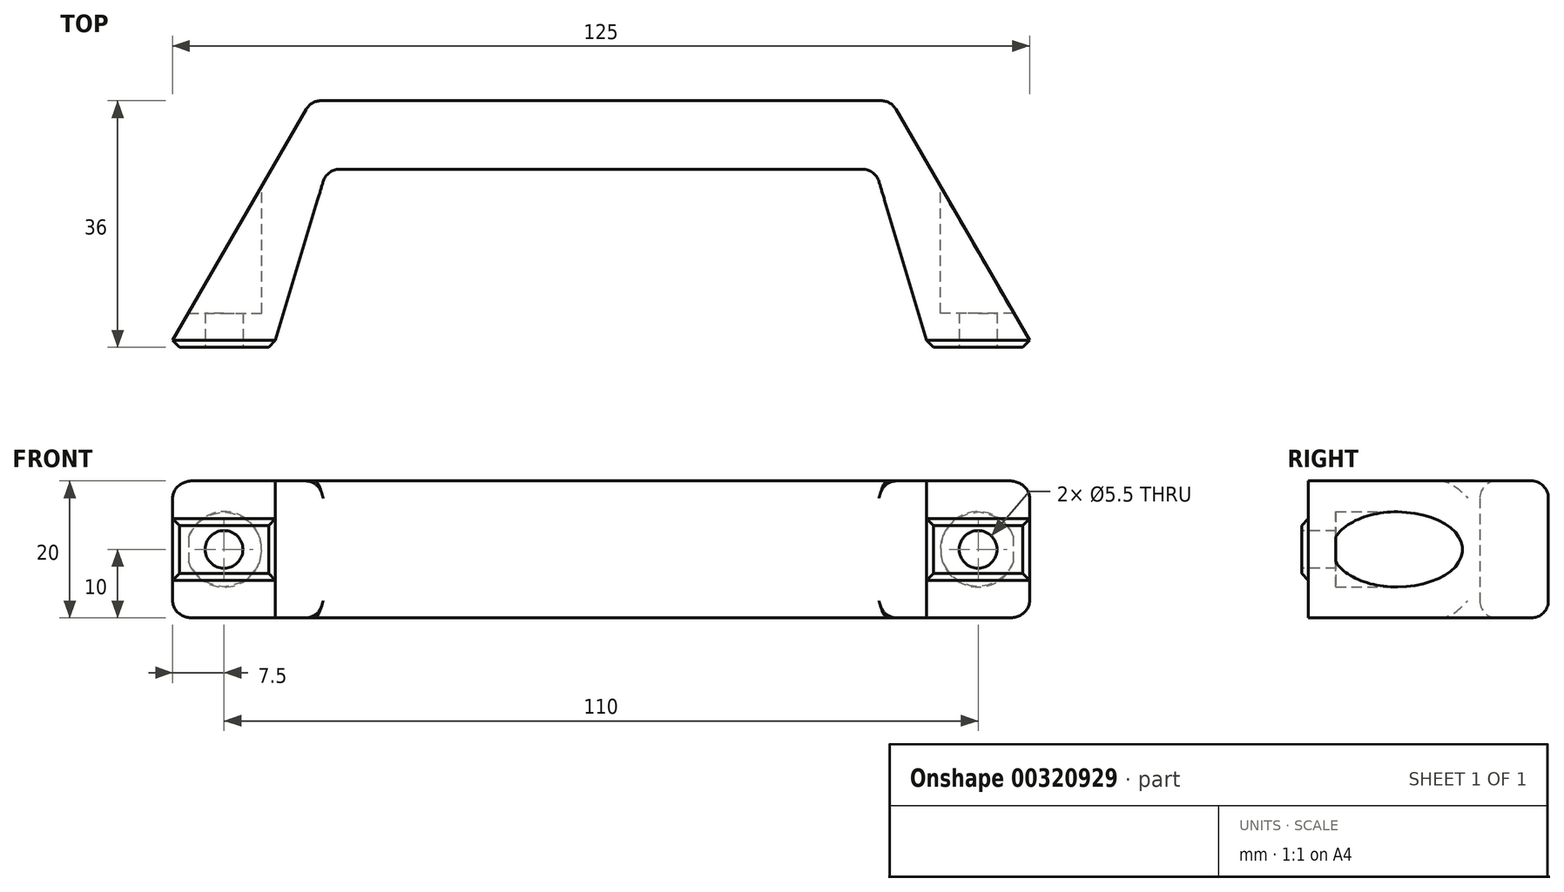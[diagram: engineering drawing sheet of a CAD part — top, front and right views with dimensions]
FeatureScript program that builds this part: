
annotation { "Feature Type Name" : "Feature", "Feature Type Description" : "" }
export const myFeature = defineFeature(function(context is Context, id is Id, definition is map)
    precondition{}
    {
        {
            var Q0;
            Q0=qCreatedBy(makeId("Top.planeOp"),FACE);
            var sketch = newSketch(context, id + "F0", { "sketchPlane" : qUnion([Q0])});
            skLineSegment(sketch, "E0", {"start": v(0, 0) * mm, "end": v(20.2, 35) * mm});
            skLineSegment(sketch, "E1", {"start": v(20.2, 35) * mm, "end": v(104.8, 35) * mm});
            skLineSegment(sketch, "E2", {"start": v(104.8, 35) * mm, "end": v(125, 0) * mm});
            skLineSegment(sketch, "E3", {"start": v(102.5, 25) * mm, "end": v(22.5, 25) * mm});
            skLineSegment(sketch, "E4", {"start": v(0, 0) * mm, "end": v(15, 0) * mm});
            skLineSegment(sketch, "E5", {"start": v(15, 0) * mm, "end": v(22.5, 25) * mm});
            skLineSegment(sketch, "E6", {"start": v(125, 0) * mm, "end": v(110, 0) * mm});
            skLineSegment(sketch, "E7", {"start": v(110, 0) * mm, "end": v(102.5, 25) * mm});
            skSolve(sketch);
        }
        {
            var Q0;
            Q0 = qSketchRegion(id + "F0", true);
            extrude(context, id + "F1", {"entities" : qUnion([Q0]), "depth" : 20 * mm});
        }
        {
            var Q0;
            Q0=makeQuery(id+"F1.opExtrude","SWEPT_FACE",FACE,{"disambiguationData":[OSD([sQuery(id+"F0.wireOp",EDGE,"E6")])]});
            var sketch = newSketch(context, id + "F2", { "sketchPlane" : qUnion([Q0])});
            skLineSegment(sketch, "E8.0.0", {"start": v(110, 0) * mm, "end": v(125, 0) * mm, "construction": true});
            skLineSegment(sketch, "E8.0.1", {"start": v(125, 0) * mm, "end": v(125, 20) * mm, "construction": true});
            skLineSegment(sketch, "E8.0.2", {"start": v(125, 20) * mm, "end": v(110, 20) * mm, "construction": true});
            skLineSegment(sketch, "E8.0.3", {"start": v(110, 20) * mm, "end": v(110, 0) * mm, "construction": true});
            skLineSegment(sketch, "E9.0.0", {"start": v(0, 0) * mm, "end": v(15, 0) * mm, "construction": true});
            skLineSegment(sketch, "E9.0.1", {"start": v(15, 0) * mm, "end": v(15, 20) * mm, "construction": true});
            skLineSegment(sketch, "E9.0.2", {"start": v(15, 20) * mm, "end": v(0, 20) * mm, "construction": true});
            skLineSegment(sketch, "E9.0.3", {"start": v(0, 20) * mm, "end": v(0, 0) * mm, "construction": true});
            skLineSegment(sketch, "E10.bottom", {"start": v(0, 14.5) * mm, "end": v(15, 14.5) * mm});
            skLineSegment(sketch, "E10.top", {"start": v(0, 5.5) * mm, "end": v(15, 5.5) * mm});
            skLineSegment(sketch, "E10.left", {"start": v(0, 14.5) * mm, "end": v(0, 5.5) * mm});
            skLineSegment(sketch, "E10.right", {"start": v(15, 14.5) * mm, "end": v(15, 5.5) * mm});
            skLineSegment(sketch, "E11.bottom", {"start": v(110, 14.5) * mm, "end": v(125, 14.5) * mm});
            skLineSegment(sketch, "E11.top", {"start": v(110, 5.5) * mm, "end": v(125, 5.5) * mm});
            skLineSegment(sketch, "E11.left", {"start": v(110, 14.5) * mm, "end": v(110, 5.5) * mm});
            skLineSegment(sketch, "E11.right", {"start": v(125, 14.5) * mm, "end": v(125, 5.5) * mm});
            skSolve(sketch);
        }
        {
            var Q0;
            Q0 = qSketchRegion(id + "F2", true);
            extrude(context, id + "F3", {"entities" : qUnion([Q0]), "operationType" : NewBodyOperationType.ADD, "depth" : 1 * mm});
        }
        {
            var Q0;
            Q0=makeQuery(id+"F3.opExtrude","CAP_FACE",FACE,{"disambiguationData":[OSD([sQuery(id+"F2.wireOp",EDGE,"E10.bottom"),sQuery(id+"F2.wireOp",EDGE,"E10.top"),sQuery(id+"F2.wireOp",EDGE,"E10.left"),sQuery(id+"F2.wireOp",EDGE,"E10.right")])],"isStart":false});
            var sketch = newSketch(context, id + "F4", { "sketchPlane" : qUnion([Q0])});
            skLineSegment(sketch, "E12.0.0", {"start": v(0, 14.5) * mm, "end": v(0, 5.5) * mm, "construction": true});
            skLineSegment(sketch, "E12.0.1", {"start": v(0, 5.5) * mm, "end": v(15, 5.5) * mm, "construction": true});
            skLineSegment(sketch, "E12.0.2", {"start": v(15, 5.5) * mm, "end": v(15, 14.5) * mm, "construction": true});
            skLineSegment(sketch, "E12.0.3", {"start": v(15, 14.5) * mm, "end": v(0, 14.5) * mm, "construction": true});
            skLineSegment(sketch, "E13.0.0", {"start": v(110, 14.5) * mm, "end": v(110, 5.5) * mm, "construction": true});
            skLineSegment(sketch, "E13.0.1", {"start": v(110, 5.5) * mm, "end": v(125, 5.5) * mm, "construction": true});
            skLineSegment(sketch, "E13.0.2", {"start": v(125, 5.5) * mm, "end": v(125, 14.5) * mm, "construction": true});
            skLineSegment(sketch, "E13.0.3", {"start": v(125, 14.5) * mm, "end": v(110, 14.5) * mm, "construction": true});
            skCircle(sketch, "E14", {"center": v(7.5, 10) * mm, "radius": 2.75 * mm});
            skPoint(sketch, "E14.centerSnap0", {"position": v(15, 10) * mm});
            skPoint(sketch, "E14.centerSnap1", {"position": v(7.5, 14.5) * mm});
            skCircle(sketch, "E15", {"center": v(117.5, 10) * mm, "radius": 2.75 * mm});
            skPoint(sketch, "E15.centerSnap0", {"position": v(110, 10) * mm});
            skPoint(sketch, "E15.centerSnap1", {"position": v(117.5, 14.5) * mm});
            skSolve(sketch);
        }
        {
            var Q0;
            Q0 = qSketchRegion(id + "F4", true);
            extrude(context, id + "F5", {"entities" : qUnion([Q0]), "operationType" : NewBodyOperationType.REMOVE, "endBound" : BoundingType.THROUGH_ALL, "oppositeDirection" : true, "depth" : 25 * mm});
        }
        {
            var Q0;
            Q0=makeQuery(id+"F1.opExtrude","SWEPT_FACE",FACE,{"disambiguationData":[OSD([sQuery(id+"F0.wireOp",EDGE,"E1")])]});
            var sketch = newSketch(context, id + "F6", { "sketchPlane" : qUnion([Q0])});
            skCircle(sketch, "E16.0", {"center": v(-117.5, 10) * mm, "radius": 2.75 * mm, "construction": true});
            skCircle(sketch, "E17.0", {"center": v(-7.5, 10) * mm, "radius": 2.75 * mm, "construction": true});
            skCircle(sketch, "E18", {"center": v(-117.5, 10) * mm, "radius": 5.5 * mm});
            skCircle(sketch, "E19", {"center": v(-7.5, 10) * mm, "radius": 5.5 * mm});
            skSolve(sketch);
        }
        {
            var Q0;
            Q0 = qSketchRegion(id + "F6", true);
            extrude(context, id + "F7", {"entities" : qUnion([Q0]), "operationType" : NewBodyOperationType.REMOVE, "oppositeDirection" : true, "depth" : 31 * mm});
        }
        {
            var Q0;
            Q0=makeQuery(id+"F1.opExtrude","SWEPT_FACE",FACE,{"disambiguationData":[OSD([sQuery(id+"F0.wireOp",EDGE,"E3")])]});
            var Q1;
            Q1=makeQuery(id+"F1.opExtrude","SWEPT_FACE",FACE,{"disambiguationData":[OSD([sQuery(id+"F0.wireOp",EDGE,"E1")])]});
            var Q2;
            Q2=makeQuery(id+"F1.opExtrude","CAP_EDGE",EDGE,{"disambiguationData":[OSD([sQuery(id+"F0.wireOp",EDGE,"E2")])],"isStart":false});
            var Q3;
            Q3=makeQuery(id+"F1.opExtrude","CAP_EDGE",EDGE,{"disambiguationData":[OSD([sQuery(id+"F0.wireOp",EDGE,"E2")])],"isStart":true});
            var Q4;
            Q4=makeQuery(id+"F1.opExtrude","CAP_EDGE",EDGE,{"disambiguationData":[OSD([sQuery(id+"F0.wireOp",EDGE,"E0")])],"isStart":false});
            var Q5;
            Q5=makeQuery(id+"F1.opExtrude","CAP_EDGE",EDGE,{"disambiguationData":[OSD([sQuery(id+"F0.wireOp",EDGE,"E0")])],"isStart":true});
            fillet(context, id + "F8", {"entities" : qUnion([Q0, Q1, Q2, Q3, Q4, Q5]), "radius" : 2.5 * mm, "tangentPropagation" : true, "allowEdgeOverflow" : false});
        }
        {
            var Q0;
            Q0=makeQuery(id+"F3.opExtrude","CAP_EDGE",EDGE,{"disambiguationData":[OSD([sQuery(id+"F2.wireOp",EDGE,"E10.bottom")])],"isStart":false});
            var Q1;
            Q1=makeQuery(id+"F3.opExtrude","CAP_EDGE",EDGE,{"disambiguationData":[OSD([sQuery(id+"F2.wireOp",EDGE,"E10.left")])],"isStart":false});
            var Q2;
            Q2=makeQuery(id+"F3.opExtrude","CAP_EDGE",EDGE,{"disambiguationData":[OSD([sQuery(id+"F2.wireOp",EDGE,"E10.top")])],"isStart":false});
            var Q3;
            Q3=makeQuery(id+"F3.opExtrude","CAP_EDGE",EDGE,{"disambiguationData":[OSD([sQuery(id+"F2.wireOp",EDGE,"E10.right")])],"isStart":false});
            var Q4;
            Q4=makeQuery(id+"F3.opExtrude","CAP_EDGE",EDGE,{"disambiguationData":[OSD([sQuery(id+"F2.wireOp",EDGE,"E11.bottom")])],"isStart":false});
            var Q5;
            Q5=makeQuery(id+"F3.opExtrude","CAP_EDGE",EDGE,{"disambiguationData":[OSD([sQuery(id+"F2.wireOp",EDGE,"E11.left")])],"isStart":false});
            var Q6;
            Q6=makeQuery(id+"F3.opExtrude","CAP_EDGE",EDGE,{"disambiguationData":[OSD([sQuery(id+"F2.wireOp",EDGE,"E11.top")])],"isStart":false});
            var Q7;
            Q7=makeQuery(id+"F3.opExtrude","CAP_EDGE",EDGE,{"disambiguationData":[OSD([sQuery(id+"F2.wireOp",EDGE,"E11.right")])],"isStart":false});
            chamfer(context, id + "F9", {"entities" : qUnion([Q0, Q1, Q2, Q3, Q4, Q5, Q6, Q7]), "width" : 1 * mm, "tangentPropagation" : true});
        }
    });
